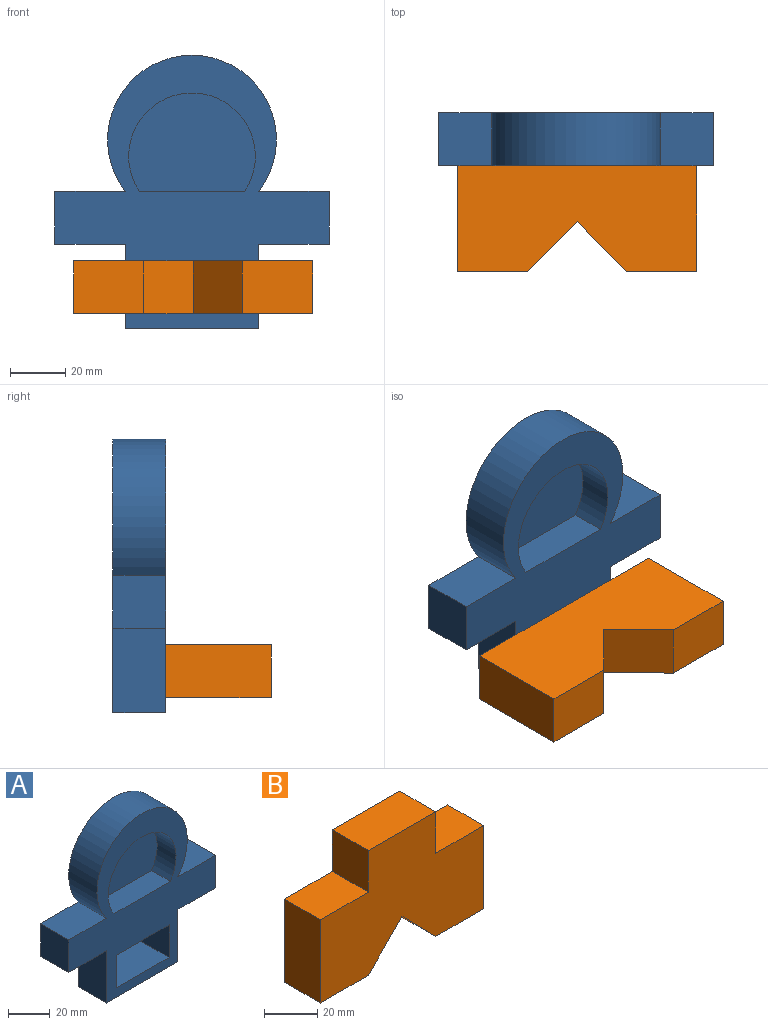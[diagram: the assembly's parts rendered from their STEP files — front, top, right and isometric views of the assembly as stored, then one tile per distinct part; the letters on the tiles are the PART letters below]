
ASSEMBLY  parts=2 mates=1
PART A: 19 faces, bbox 99x19.1x98.7 mm
  f0: plane 35.56x19.05mm, normal (0,0,1), area 677.4mm2, adj f1,f15,f16,f17
  f1: plane 19.05x19.05mm, normal (1,0,0), area 362.9mm2, adj f0,f2,f16,f17
  f2: plane 35.56x19.05mm, normal (0,0,-1), area 677.4mm2, adj f1,f15,f16,f17
  f3: plane 25.4x19.05mm, normal (0,0,1), area 483.9mm2, adj f4,f13,f16,f17
  f4: cylinder r=30.48mm len=60.96mm, axis (0,1,0), area 2589.9mm2, adj f3,f5,f16,f17
  f5: plane 25.4x19.05mm, normal (0,0,1), area 483.9mm2, adj f4,f6,f16,f17
  f6: plane 19.05x19.05mm, normal (-1,0,0), area 362.9mm2, adj f5,f7,f16,f17
  f7: plane 25.4x19.05mm, normal (0,0,-1), area 483.9mm2, adj f6,f8,f16,f17
  f8: plane 30.48x19.05mm, normal (-1,0,0), area 580.6mm2, adj f7,f9,f16,f17
  f9: plane 48.18x19.05mm, normal (0,0,-1), area 917.8mm2, adj f8,f10,f16,f17
  f10: plane 30.48x19.05mm, normal (1,0,0), area 580.6mm2, adj f9,f11,f16,f17
  f11: plane 25.4x19.05mm, normal (0,0,-1), area 483.9mm2, adj f10,f13,f16,f17
  f12: cylinder r=22.86mm len=45.72mm, axis (0,1,0), area 1254mm2, adj f14,f16,f18
  f13: plane 19.05x19.05mm, normal (1,0,0), area 362.9mm2, adj f3,f11,f16,f17
  f14: plane 38.02x12.7mm, normal (0,0,1), area 482.9mm2, adj f12,f16,f18
  f15: plane 19.05x19.05mm, normal (-1,0,0), area 362.9mm2, adj f0,f2,f16,f17
  f16: plane 98.98x98.68mm, normal (0,-1,0), area 3828.5mm2, adj f0,f1,f2,f3,f4,f5,f6,f7
  f17: plane 98.98x98.68mm, normal (0,1,0), area 5198.5mm2, adj f0,f1,f2,f3,f4,f5,f6,f7
  f18: plane 45.72x35.56mm, normal (0,-1,0), area 1369.9mm2, adj f12,f14
PART B: 13 faces, bbox 86.4x19.1x57.2 mm
  f0: plane 35.56x19.05mm, normal (0,0,1), area 677.4mm2, adj f1,f10,f11,f12
  f1: plane 19.05x19.05mm, normal (-1,0,0), area 362.9mm2, adj f0,f2,f11,f12
  f2: plane 25.4x19.05mm, normal (0,0,1), area 483.9mm2, adj f1,f3,f11,f12
  f3: plane 38.1x19.05mm, normal (-1,0,0), area 725.8mm2, adj f2,f4,f11,f12
  f4: plane 25.4x19.05mm, normal (0,0,-1), area 483.9mm2, adj f3,f5,f11,f12
  f5: plane 19.05x18.14mm, normal (0.71,0,-0.7), area 483.9mm2, adj f4,f6,f11,f12
  f6: plane 19.05x18.14mm, normal (-0.71,0,-0.7), area 483.9mm2, adj f5,f7,f11,f12
  f7: plane 25.4x19.05mm, normal (0,0,-1), area 483.9mm2, adj f6,f8,f11,f12
  f8: plane 38.1x19.05mm, normal (1,0,0), area 725.8mm2, adj f7,f9,f11,f12
  f9: plane 25.4x19.05mm, normal (0,0,1), area 483.9mm2, adj f8,f10,f11,f12
  f10: plane 19.05x19.05mm, normal (1,0,0), area 362.9mm2, adj f0,f9,f11,f12
  f11: plane 86.36x57.15mm, normal (0,-1,0), area 3645.2mm2, adj f0,f1,f2,f3,f4,f5,f6,f7
  f12: plane 86.36x57.15mm, normal (0,1,0), area 3645.2mm2, adj f0,f1,f2,f3,f4,f5,f6,f7
PLACE A t=(-9.18,96.3,70.76)mm
PLACE B rot(axis=(-1,0,0),90deg) t=(3.66,68.61,59.23)mm
MATE fastened B.f11 <-> A.f2  axis (0,0,1) through (-18.93,96.3,78.28)mm
